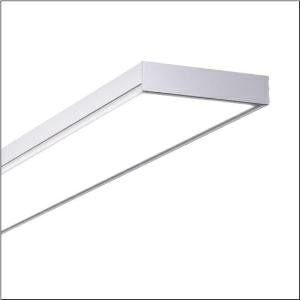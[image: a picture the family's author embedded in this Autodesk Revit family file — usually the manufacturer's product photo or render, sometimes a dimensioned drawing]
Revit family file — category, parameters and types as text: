
# Revit family: apollon_r__31_surface_51mp26wd2441e_9924
name_source: partatom
category: Lighting Fixtures
units: mm (PartAtom-declared; Revit-internal decimal feet)

## family parameters
Cut with Voids When Loaded = No
Host = Face
Light Source = No
Part Type = Normal
Room Calculation Point = No
Round Connector Dimension = Use Diameter
Shared = No

## types (1)
- Apollon® 31 Surface (1 x LED, 4600 lm, 33 W, 4000K)
    Apparent Load = 33 VA
    CIE Flux Codes = 61 87 97 97 100
    Color Rendering = 80
    Color Temperature = 4000K
    Default Elevation = 1800 mm
    Description = Apollon® 31 Surface, office luminaire, primary optical cover: micro prismatic cover, of PMMA, light emission: direct distribution, primary light characteristic: symmetric, installation type: surface-mounted, LED, rated luminous flux: 4.600lm, luminous efficacy: 139lm/W, light colour: 840, colour temperature: 4000K, control gear: ECG DALI, with terminal, 5-pole, mains connection: 220..240V, AC, 50/60Hz, rated input power: 33W, housing, of sheet steel, coil coated, metallic grey (RAL 9006), length: 1.545mm, width: 200mm, height: 44mm, protection rating (complete): IP20, insulation class (complete): insulation class II (safety insulation), certification: CE, impact resistance: IK02, permissible operating ambient temperature: -20..+40°C, standard: EN 60598-2-22, packaging unit: 1 piece
    Height = 44 mm
    Lamp = 1 x LED
    Lamp Light Flux = 4600 lm
    Lamp Power = 33 W
    Lamp count = 1
    Length = 1545 mm
    Luminous efficacy = 139 lm/W
    Manufacturer = Siteco
    ModVariant = No
    Model = 51MP26WD2441E
    Mounting Place = Ceiling
    Mounting Type = Surface mounted
    Number of Poles = 1
    OnlyDefault = Yes
    Power Factor = 1
    Product Name = Apollon® 31 Surface
    Product group = office luminaire | ceiling mounted
    ProductGroupID = 304
    Protection Class = Protection class II
    Protection Degree = IP 20
    RLX_Detail_Level = 1
    RLX_Emergency_Light_Flux = 0 lm
    RLX_Emergency_Type = 0
    RLX_Emergency_Type_DB = No
    RlxData = <blob elided: 24125 chars, md5=543a1aa3>
    Socket = socket
    Standby Power = 0 W
    System Light Flux = 4600 lm
    System Power = 33 W
    Type Comments = Product without accessories
    Type Image = l_1007091.jpg
    URL = http://relux.com
    VarID = ---
    Voltage = 0 V
    Weight = 0.00 kg
    Width = 200 mm  [stored 0.656168 ft]

note: [stored X ft] marks values corroborated as IEEE doubles in the binary element streams (Revit-internal decimal feet)

## geometry (parser evidence)
native form markers: Blend x4, Sweep x10
no freeform markers — native parametric forms only
